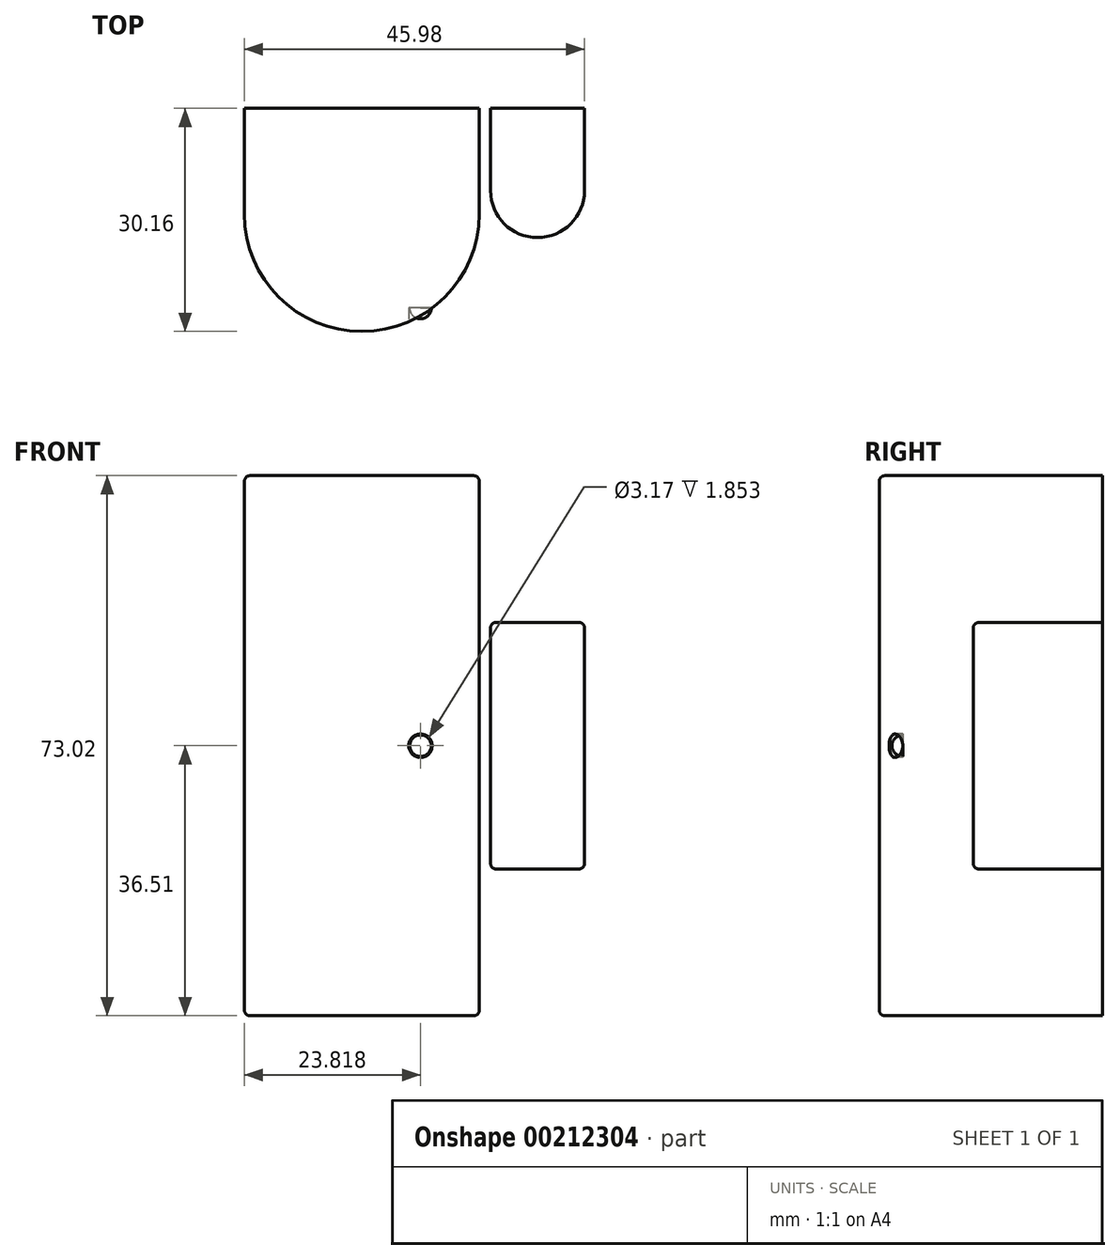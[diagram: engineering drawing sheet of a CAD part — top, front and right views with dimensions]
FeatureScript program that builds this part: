
annotation { "Feature Type Name" : "Feature", "Feature Type Description" : "" }
export const myFeature = defineFeature(function(context is Context, id is Id, definition is map)
    precondition{}
    {
        {
            var Q0;
            Q0=qCreatedBy(makeId("Top.planeOp"),FACE);
            var sketch = newSketch(context, id + "F0", { "sketchPlane" : qUnion([Q0])});
            skLineSegment(sketch, "E0.bottom", {"start": v(-15.88, 0) * mm, "end": v(15.88, 0) * mm});
            skLineSegment(sketch, "E0.top", {"start": v(-15.88, -14.29) * mm, "end": v(15.88, -14.29) * mm, "construction": true});
            skLineSegment(sketch, "E0.left", {"start": v(-15.88, 0) * mm, "end": v(-15.88, -14.29) * mm});
            skLineSegment(sketch, "E0.right", {"start": v(15.88, 0) * mm, "end": v(15.87, -14.29) * mm});
            skArc(sketch, "E1", {"start": v(-15.88, -14.29) * mm, "mid": v(0, -30.16) * mm, "end": v(15.88, -14.29) * mm});
            skSolve(sketch);
        }
        {
            var Q0;
            Q0 = qSketchRegion(id + "F0", true);
            extrude(context, id + "F1", {"entities" : qUnion([Q0]), "endBound" : BoundingType.SYMMETRIC, "depth" : 73.02 * mm});
        }
        {
            var Q0;
            Q0=makeQuery(id+"F1.opExtrude","CAP_EDGE",EDGE,{"disambiguationData":[OSD([sQuery(id+"F0.wireOp",EDGE,"E1")])],"isStart":false});
            cPoint(context, id + "F2", {"entities" : qUnion([Q0]), "parameter" : 0.5});
        }
        {
            var Q0;
            Q0=qCreatedBy(makeId("Front.planeOp"),FACE);
            var Q1;
            Q1 = qCreatedBy(id + "F2" ,VERTEX);
            cPlane(context, id + "F3", {"entities" : qUnion([Q0, Q1]), "cplaneType" : CPlaneType.PLANE_POINT, "offset" : 25.4 * mm, "width" : 152.4 * mm, "height" : 152.4 * mm});
        }
        {
            var Q0;
            Q0=qCreatedBy(id+"F3.planeOp",FACE);
            var sketch = newSketch(context, id + "F4", { "sketchPlane" : qUnion([Q0])});
            skCircle(sketch, "E2", {"center": v(7.94, 0) * mm, "radius": 1.59 * mm});
            skLineSegment(sketch, "E3", {"start": v(0, 0) * mm, "end": v(7.94, 0) * mm, "construction": true});
            skSolve(sketch);
        }
        {
            var Q0;
            Q0 = qSketchRegion(id + "F4", true);
            extrude(context, id + "F5", {"entities" : qUnion([Q0]), "operationType" : NewBodyOperationType.REMOVE, "oppositeDirection" : true, "depth" : 3.17 * mm});
        }
        {
            var Q0;
            Q0=makeQuery(id+"F5.boolean.opBoolean","COPY",FACE,{"derivedFrom":makeQuery(id+"F5.opExtrude","CAP_FACE",FACE,{"disambiguationData":[OSD([sQuery(id+"F4.wireOp",EDGE,"E2")])],"isStart":false})});
            var sketch = newSketch(context, id + "F6", { "sketchPlane" : qUnion([Q0])});
            skArc(sketch, "E4.0", {"start": v(7.94, 1.46) * mm, "mid": v(6.48, 0) * mm, "end": v(7.94, -1.46) * mm});
            skLineSegment(sketch, "E5", {"start": v(7.94, 1.46) * mm, "end": v(7.94, -1.46) * mm});
            skSolve(sketch);
        }
        {
            var Q0;
            Q0 = qSketchRegion(id + "F6", true);
            var Q1;
            Q1=sQuery(id+"F6.wireOp",EDGE,"E5");
            revolve(context, id + "F7", {"operationType" : NewBodyOperationType.ADD, "entities" : qUnion([Q0]), "axis" : qUnion([Q1]), "revolveType" : RevolveType.FULL});
        }
        {
            var Q0;
            Q0=makeQuery(id+"F1.opExtrude","CAP_EDGE",EDGE,{"disambiguationData":[OSD([sQuery(id+"F0.wireOp",EDGE,"E1")])],"isStart":false});
            var Q1;
            Q1=makeQuery(id+"F1.opExtrude","CAP_EDGE",EDGE,{"disambiguationData":[OSD([sQuery(id+"F0.wireOp",EDGE,"E1")])],"isStart":true});
            fillet(context, id + "F8", {"entities" : qUnion([Q0, Q1]), "radius" : 0.76 * mm, "tangentPropagation" : true, "allowEdgeOverflow" : false});
        }
        {
            var Q0;
            Q0=qCreatedBy(makeId("Top.planeOp"),FACE);
            var sketch = newSketch(context, id + "F9", { "sketchPlane" : qUnion([Q0])});
            skLineSegment(sketch, "E6.bottom", {"start": v(17.4, 0) * mm, "end": v(30.1, 0) * mm});
            skLineSegment(sketch, "E6.top", {"start": v(17.4, -11.11) * mm, "end": v(30.1, -11.11) * mm, "construction": true});
            skLineSegment(sketch, "E6.left", {"start": v(17.4, 0) * mm, "end": v(17.4, -11.11) * mm});
            skLineSegment(sketch, "E6.right", {"start": v(30.1, 0) * mm, "end": v(30.1, -11.11) * mm});
            skArc(sketch, "E7", {"start": v(17.4, -11.11) * mm, "mid": v(23.75, -17.46) * mm, "end": v(30.1, -11.11) * mm});
            skSolve(sketch);
        }
        {
            var Q0;
            Q0 = qSketchRegion(id + "F9", true);
            extrude(context, id + "F10", {"entities" : qUnion([Q0]), "endBound" : BoundingType.SYMMETRIC, "depth" : 33.34 * mm});
        }
        {
            var Q0;
            Q0=makeQuery(id+"F10.opExtrude","CAP_EDGE",EDGE,{"disambiguationData":[OSD([sQuery(id+"F9.wireOp",EDGE,"E7")])],"isStart":false});
            var Q1;
            Q1=makeQuery(id+"F10.opExtrude","CAP_EDGE",EDGE,{"disambiguationData":[OSD([sQuery(id+"F9.wireOp",EDGE,"E7")])],"isStart":true});
            fillet(context, id + "F11", {"entities" : qUnion([Q0, Q1]), "radius" : 0.76 * mm, "tangentPropagation" : true, "allowEdgeOverflow" : false});
        }
    });
